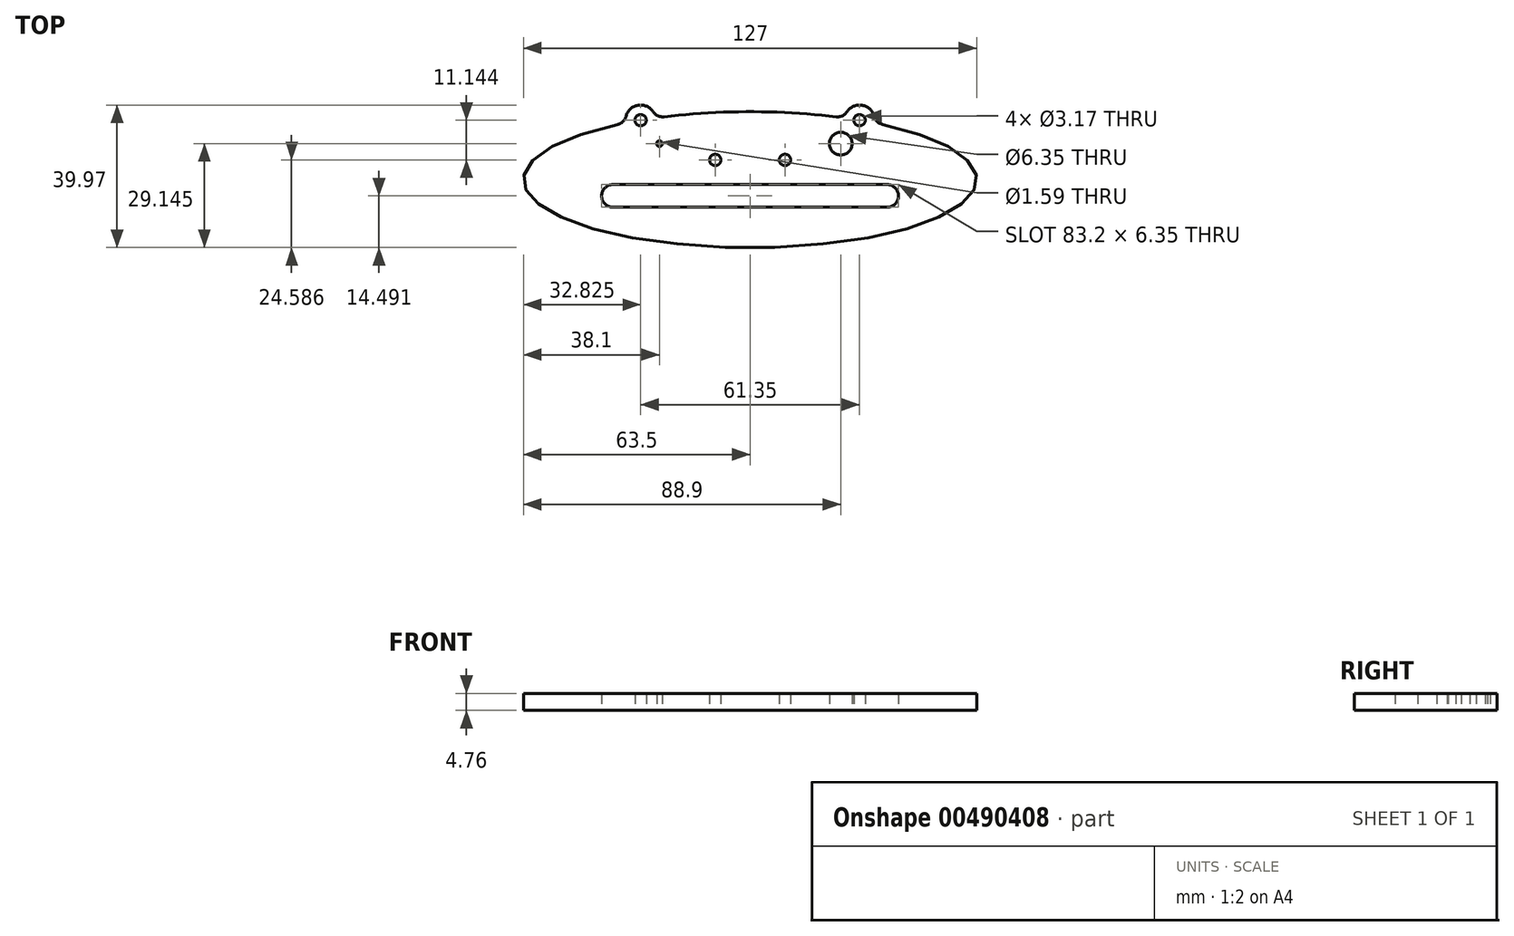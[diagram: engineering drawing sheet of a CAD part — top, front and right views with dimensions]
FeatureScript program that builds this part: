
annotation { "Feature Type Name" : "Feature", "Feature Type Description" : "" }
export const myFeature = defineFeature(function(context is Context, id is Id, definition is map)
    precondition{}
    {
        {
            var Q0;
            Q0=qCreatedBy(makeId("Top.planeOp"),FACE);
            var sketch = newSketch(context, id + "F0", { "sketchPlane" : qUnion([Q0])});
            skArc(sketch, "E0", {"start": v(-27.14, 19.02) * mm, "mid": v(-31.37, 20.86) * mm, "end": v(-34.78, 17.75) * mm});
            skCircle(sketch, "E1", {"center": v(-25.4, 10.1) * mm, "radius": 3.18 * mm});
            skArc(sketch, "E2", {"start": v(-5.9, 8.07) * mm, "mid": v(-11.1, 9.97) * mm, "end": v(-14.4, 5.54) * mm});
            skArc(sketch, "E3.MirrorC", {"start": v(5.9, 8.07) * mm, "mid": v(11.1, 9.97) * mm, "end": v(14.4, 5.54) * mm});
            skCircle(sketch, "E4.MirrorC", {"center": v(25.4, 10.1) * mm, "radius": 3.18 * mm});
            skArc(sketch, "E5.MirrorC", {"start": v(27.14, 19.02) * mm, "mid": v(31.37, 20.86) * mm, "end": v(34.78, 17.75) * mm});
            skLineSegment(sketch, "E6.0", {"start": v(-38.43, -10.9) * mm, "end": v(38.43, -10.9) * mm});
            skLineSegment(sketch, "E7.0", {"start": v(-38.43, 1.8) * mm, "end": v(-14.4, 1.8) * mm});
            skArc(sketch, "E8.trimOffspring", {"start": v(38.43, 1.8) * mm, "mid": v(44.78, -4.56) * mm, "end": v(38.43, -10.9) * mm});
            skArc(sketch, "E9.trimOffspring", {"start": v(-38.43, 1.8) * mm, "mid": v(-44.78, -4.56) * mm, "end": v(-38.43, -10.9) * mm});
            skCircle(sketch, "E10", {"center": v(-9.77, 5.54) * mm, "radius": 1.59 * mm});
            skCircle(sketch, "E11", {"center": v(9.77, 5.54) * mm, "radius": 1.59 * mm});
            skCircle(sketch, "E12", {"center": v(-25.4, 10.1) * mm, "radius": 0.8 * mm});
            skCircle(sketch, "E13", {"center": v(25.4, 10.1) * mm, "radius": 0.8 * mm});
            skCircle(sketch, "E14", {"center": v(-30.68, 16.68) * mm, "radius": 1.59 * mm});
            skCircle(sketch, "E15", {"center": v(30.68, 16.68) * mm, "radius": 1.59 * mm});
            skLineSegment(sketch, "E16", {"start": v(14.4, 5.54) * mm, "end": v(14.4, 1.8) * mm});
            skLineSegment(sketch, "E17", {"start": v(-14.4, 5.54) * mm, "end": v(-14.4, 1.8) * mm});
            skEllipticalArc(sketch, "E18.trimOffspring", {});
            skEllipticalArc(sketch, "E19.trimOffspring", {});
            skPoint(sketch, "E20.visualSharp", {"position": v(-26.48, 17.31) * mm});
            skArc(sketch, "E20.filletArc", {"start": v(-27.14, 19.02) * mm, "mid": v(-25.82, 17.9) * mm, "end": v(-24.1, 17.62) * mm});
            skPoint(sketch, "E21.visualSharp", {"position": v(-34.85, 15.92) * mm});
            skArc(sketch, "E21.filletArc", {"start": v(-37.18, 15.44) * mm, "mid": v(-35.66, 16.26) * mm, "end": v(-34.78, 17.75) * mm});
            skPoint(sketch, "E22.visualSharp", {"position": v(26.48, 17.31) * mm});
            skArc(sketch, "E22.filletArc", {"start": v(24.1, 17.62) * mm, "mid": v(25.82, 17.9) * mm, "end": v(27.14, 19.02) * mm});
            skPoint(sketch, "E23.visualSharp", {"position": v(34.85, 15.92) * mm});
            skArc(sketch, "E23.filletArc", {"start": v(34.78, 17.75) * mm, "mid": v(35.66, 16.26) * mm, "end": v(37.18, 15.44) * mm});
            skArc(sketch, "E24", {"start": v(-5.9, 8.07) * mm, "mid": v(0, 5.88) * mm, "end": v(5.9, 8.07) * mm});
            skLineSegment(sketch, "E25.trimOffspring", {"start": v(14.4, 1.8) * mm, "end": v(38.43, 1.8) * mm});
            skLineSegment(sketch, "E26.0", {"start": v(-38.43, -1.38) * mm, "end": v(38.43, -1.38) * mm});
            skArc(sketch, "E26.1", {"start": v(-38.43, -1.38) * mm, "mid": v(-41.6, -4.56) * mm, "end": v(-38.43, -7.73) * mm});
            skLineSegment(sketch, "E26.2", {"start": v(-38.43, -7.73) * mm, "end": v(38.43, -7.73) * mm});
            skArc(sketch, "E26.3", {"start": v(38.43, -1.38) * mm, "mid": v(41.6, -4.56) * mm, "end": v(38.43, -7.73) * mm});
            const initialGuessF0  = {"E18.trimOffspring": [0, 0, -1, 0, 0.0635, 0.01905, 4.323051576797765, 5.101726383971582], "E19.trimOffspring": [0, 0, -1, 0, 0.0635, 0.01905, 5.337931062507581, 4.086846898261799]};
            skSetInitialGuess(sketch, initialGuessF0);
            skSolve(sketch);
        }
        {
            var Q0;
            Q0=makeQuery(id+"F0.imprint","IMPRINT",FACE,{"disambiguationData":[TD([[makeQuery(id+"F0.imprint","IMPRINT",EDGE,{"derivedFrom":sQuery(id+"F0.wireOp",EDGE,"E2")}),1.0]])]});
            extrude(context, id + "F1", {"entities" : qUnion([Q0]), "depth" : 4.76 * mm});
        }
        {
            var Q0;
            Q0 = qSketchRegion(id + "F0", true);
            extrude(context, id + "F2", {"entities" : qUnion([Q0]), "operationType" : NewBodyOperationType.ADD, "depth" : 3.17 * mm});
        }
        {
            var Q0;
            Q0=makeQuery(id+"F0.imprint","IMPRINT",FACE,{"disambiguationData":[TD([[makeQuery(id+"F0.imprint","IMPRINT",EDGE,{"derivedFrom":sQuery(id+"F0.wireOp",EDGE,"E1")}),1.0]])]});
            var Q1;
            Q1=makeQuery(id+"F0.imprint","IMPRINT",FACE,{"disambiguationData":[TD([[makeQuery(id+"F0.imprint","IMPRINT",EDGE,{"derivedFrom":sQuery(id+"F0.wireOp",EDGE,"E4.MirrorC")}),-1.0]])]});
            extrude(context, id + "F3", {"entities" : qUnion([Q0, Q1]), "operationType" : NewBodyOperationType.ADD, "depth" : 4.76 * mm});
        }
    });
